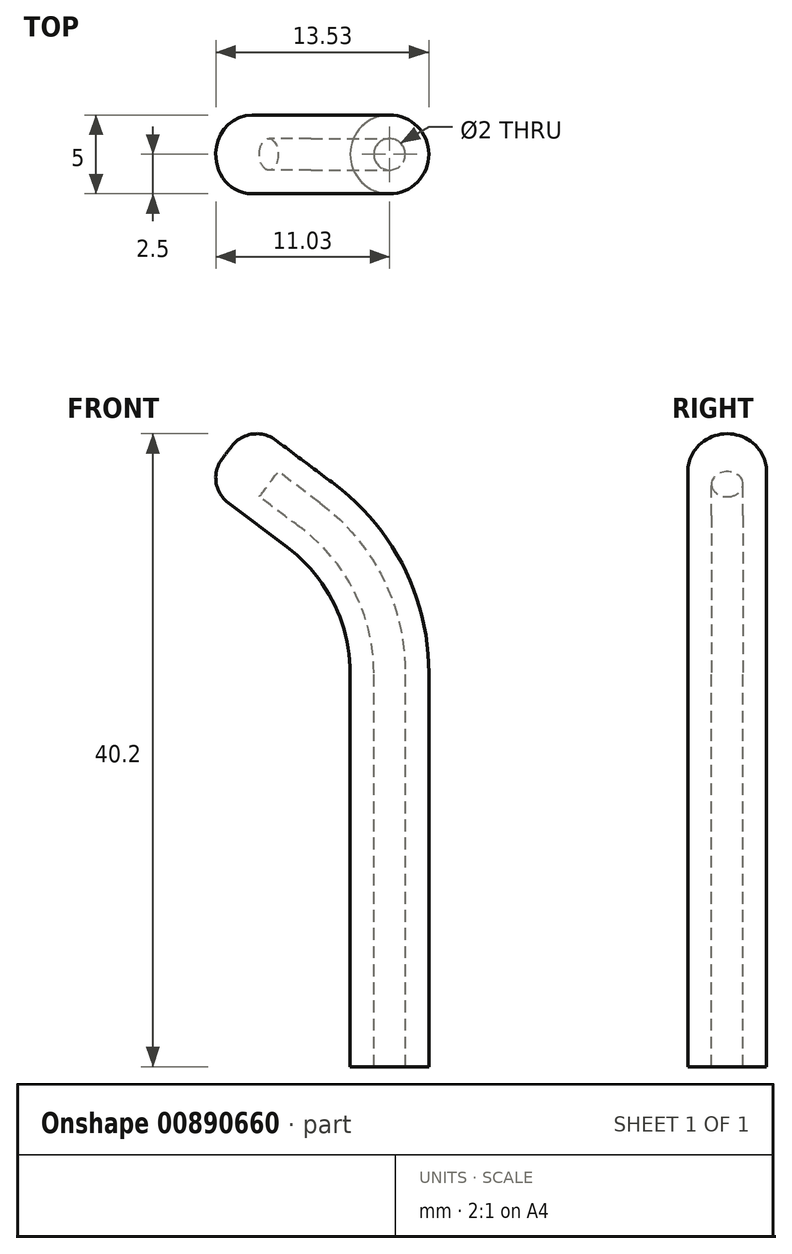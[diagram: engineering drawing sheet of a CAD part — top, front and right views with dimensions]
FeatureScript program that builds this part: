
annotation { "Feature Type Name" : "Feature", "Feature Type Description" : "" }
export const myFeature = defineFeature(function(context is Context, id is Id, definition is map)
    precondition{}
    {
        {
            var Q0;
            Q0=qCreatedBy(makeId("Front.planeOp"),FACE);
            var sketch = newSketch(context, id + "F0", { "sketchPlane" : qUnion([Q0])});
            skLineSegment(sketch, "E0", {"start": v(0, 0) * mm, "end": v(0, 25) * mm});
            skArc(sketch, "E1", {"start": v(0, 25) * mm, "mid": v(-1.32, 30.6) * mm, "end": v(-5, 35) * mm});
            skLineSegment(sketch, "E2", {"start": v(-5, 35) * mm, "end": v(-10.33, 39) * mm});
            skSolve(sketch);
        }
        {
            var Q0;
            Q0=qCreatedBy(makeId("Top.planeOp"),FACE);
            var sketch = newSketch(context, id + "F1", { "sketchPlane" : qUnion([Q0])});
            skCircle(sketch, "E3", {"center": v(0, 0) * mm, "radius": 2.5 * mm});
            skSolve(sketch);
        }
        {
            var Q0;
            Q0=makeQuery(id+"F1.imprint","IMPRINT",FACE,{"disambiguationData":[TD([[makeQuery(id+"F1.imprint","IMPRINT",EDGE,{"derivedFrom":sQuery(id+"F1.wireOp",EDGE,"E3")}),1.0]])]});
            var Q1;
            Q1=sQuery(id+"F0.wireOp",EDGE,"E0");
            var Q2;
            Q2=sQuery(id+"F0.wireOp",EDGE,"E1");
            var Q3;
            Q3=sQuery(id+"F0.wireOp",EDGE,"E2");
            sweep(context, id + "F2", {"profiles" : qUnion([Q0]), "path" : qUnion([Q1, Q2, Q3])});
        }
        {
            var Q0;
            Q0=makeQuery(id+"F2.opSweep","CAP_EDGE",EDGE,{"disambiguationData":[OSD([sQuery(id+"F0.wireOp",VERTEX,"E2.end"),sQuery(id+"F1.wireOp",EDGE,"E3")])],"isStart":false});
            fillet(context, id + "F3", {"entities" : qUnion([Q0]), "radius" : 2 * mm, "tangentPropagation" : true, "allowEdgeOverflow" : false});
        }
        {
            var Q0;
            Q0=qCreatedBy(makeId("Front.planeOp"),FACE);
            var sketch = newSketch(context, id + "F4", { "sketchPlane" : qUnion([Q0])});
            skLineSegment(sketch, "E4", {"start": v(0, 0) * mm, "end": v(0, 25) * mm});
            skArc(sketch, "E5", {"start": v(0, 25) * mm, "mid": v(-1.32, 30.6) * mm, "end": v(-5, 35) * mm});
            skLineSegment(sketch, "E6", {"start": v(-5, 35) * mm, "end": v(-7.67, 37) * mm});
            skSolve(sketch);
        }
        {
            var Q0;
            Q0=makeQuery(id+"F2.opSweep","CAP_FACE",FACE,{"disambiguationData":[OSD([sQuery(id+"F0.wireOp",VERTEX,"E0.start"),sQuery(id+"F1.wireOp",EDGE,"E3")])],"isStart":true});
            var sketch = newSketch(context, id + "F5", { "sketchPlane" : qUnion([Q0])});
            skCircle(sketch, "E7", {"center": v(0, 0) * mm, "radius": 1 * mm});
            skSolve(sketch);
        }
        {
            var Q0;
            Q0 = qSketchRegion(id + "F5", true);
            var Q1;
            Q1=sQuery(id+"F4.wireOp",EDGE,"E4");
            var Q2;
            Q2=sQuery(id+"F4.wireOp",EDGE,"E5");
            var Q3;
            Q3=sQuery(id+"F4.wireOp",EDGE,"E6");
            sweep(context, id + "F6", {"operationType" : NewBodyOperationType.REMOVE, "profiles" : qUnion([Q0]), "path" : qUnion([Q1, Q2, Q3])});
        }
    });
